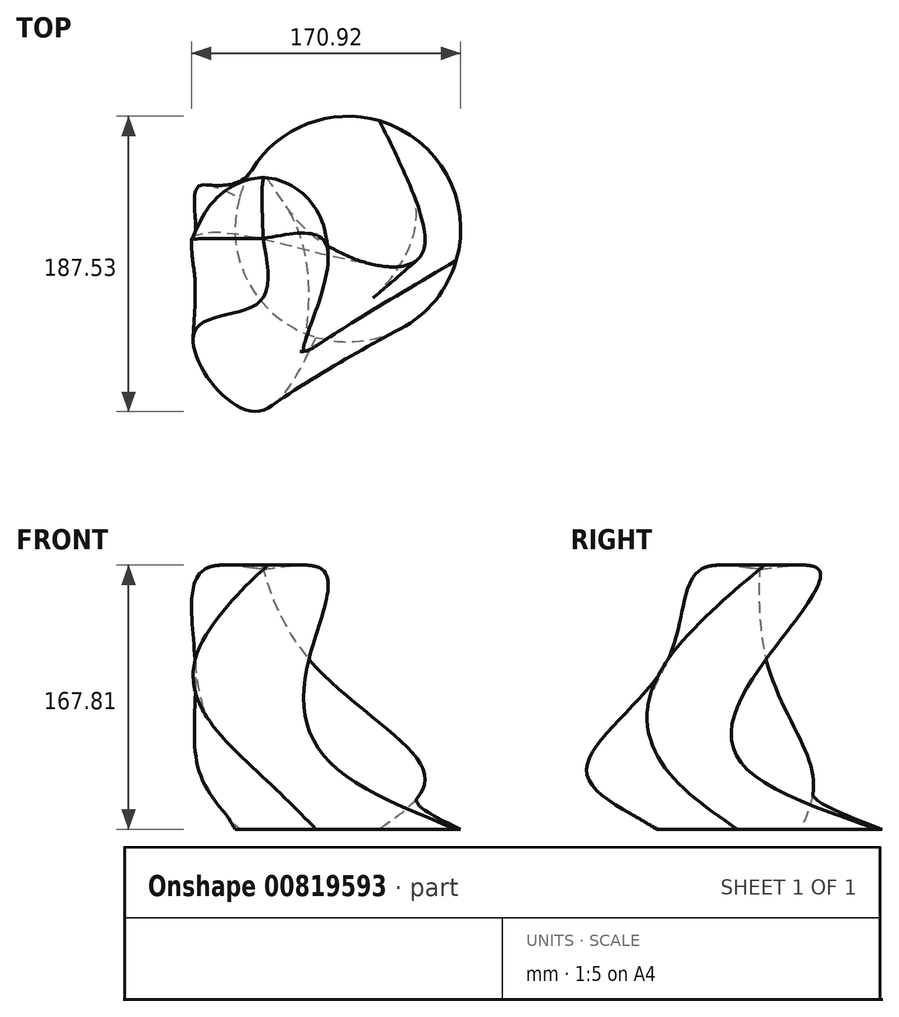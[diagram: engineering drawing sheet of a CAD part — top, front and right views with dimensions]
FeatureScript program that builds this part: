
annotation { "Feature Type Name" : "Feature", "Feature Type Description" : "" }
export const myFeature = defineFeature(function(context is Context, id is Id, definition is map)
    precondition{}
    {
        {
            var Q0;
            Q0=qCreatedBy(makeId("Top.planeOp"),FACE);
            cPlane(context, id + "F0", {"entities" : qUnion([Q0]), "cplaneType" : CPlaneType.OFFSET, "offset" : 108 * mm, "oppositeDirection" : true, "width" : 150 * mm, "height" : 150 * mm});
        }
        {
            var Q0;
            Q0=qCreatedBy(makeId("Top.planeOp"),FACE);
            cPlane(context, id + "F1", {"entities" : qUnion([Q0]), "cplaneType" : CPlaneType.OFFSET, "offset" : 72 * mm, "oppositeDirection" : true, "width" : 150 * mm, "height" : 150 * mm});
        }
        {
            var Q0;
            Q0=qCreatedBy(makeId("Top.planeOp"),FACE);
            cPlane(context, id + "F2", {"entities" : qUnion([Q0]), "cplaneType" : CPlaneType.OFFSET, "offset" : 57 * mm, "width" : 150 * mm, "height" : 150 * mm});
        }
        {
            var Q0;
            Q0=qCreatedBy(id+"F2.planeOp",FACE);
            var sketch = newSketch(context, id + "F3", { "sketchPlane" : qUnion([Q0])});
            skCircle(sketch, "E0", {"center": v(0, 38.13) * mm, "radius": 37.42 * mm});
            skSolve(sketch);
        }
        {
            var Q0;
            Q0=qCreatedBy(makeId("Top.planeOp"),FACE);
            var sketch = newSketch(context, id + "F4", { "sketchPlane" : qUnion([Q0])});
            skLineSegment(sketch, "E1.bottom", {"start": v(29, 42.26) * mm, "end": v(-43.2, 42.26) * mm});
            skLineSegment(sketch, "E1.top", {"start": v(29, -19.95) * mm, "end": v(-43.2, -19.95) * mm});
            skLineSegment(sketch, "E1.left", {"start": v(29, 42.26) * mm, "end": v(29, -19.95) * mm});
            skLineSegment(sketch, "E1.right", {"start": v(-43.2, 42.26) * mm, "end": v(-43.2, -19.95) * mm});
            skSolve(sketch);
        }
        {
            var Q0;
            Q0=qCreatedBy(id+"F1.planeOp",FACE);
            var sketch = newSketch(context, id + "F5", { "sketchPlane" : qUnion([Q0])});
            skCircle(sketch, "E2.cCircle", {"center": v(19.57, 10.78) * mm, "radius": 42.75 * mm, "construction": true});
            skLineSegment(sketch, "E2.0", {"start": v(-3.12, -71.64) * mm, "end": v(-40.47, 71.64) * mm});
            skLineSegment(sketch, "E2.1", {"start": v(-40.47, 71.64) * mm, "end": v(102.3, 32.34) * mm});
            skLineSegment(sketch, "E2.2", {"start": v(102.3, 32.34) * mm, "end": v(-3.12, -71.64) * mm});
            skPoint(sketch, "E2.0.midPoint", {"position": v(-21.8, 0) * mm});
            skSolve(sketch);
        }
        {
            var Q0;
            Q0=qCreatedBy(id+"F0.planeOp",FACE);
            var sketch = newSketch(context, id + "F6", { "sketchPlane" : qUnion([Q0])});
            skCircle(sketch, "E3", {"center": v(53.74, 44.14) * mm, "radius": 71.65 * mm});
            skSolve(sketch);
        }
        {
            var Q0;
            Q0=sQuery(id+"F3.wireOp",VERTEX,"E0.center");
            var Q1;
            Q1=makeQuery(id+"F3.imprint","IMPRINT",FACE,{"disambiguationData":[TD([[makeQuery(id+"F3.imprint","IMPRINT",EDGE,{"derivedFrom":sQuery(id+"F3.wireOp",EDGE,"E0")}),1.0]])]});
            var Q2;
            Q2=makeQuery(id+"F4.imprint","IMPRINT",FACE,{"disambiguationData":[TD([[makeQuery(id+"F4.imprint","IMPRINT",EDGE,{"derivedFrom":sQuery(id+"F4.wireOp",EDGE,"E1.bottom")}),1.0]])]});
            var Q3;
            Q3=makeQuery(id+"F5.imprint","IMPRINT",FACE,{"disambiguationData":[TD([[makeQuery(id+"F5.imprint","IMPRINT",EDGE,{"derivedFrom":sQuery(id+"F5.wireOp",EDGE,"E2.0")}),-1.0]])]});
            var Q4;
            Q4=makeQuery(id+"F6.imprint","IMPRINT",FACE,{"disambiguationData":[TD([[makeQuery(id+"F6.imprint","IMPRINT",EDGE,{"derivedFrom":sQuery(id+"F6.wireOp",EDGE,"E3")}),1.0]])]});
            loft(context, id + "F7", {"sheetProfilesArray" : [{ "sheetProfileEntities" : qUnion([Q0]) }, { "sheetProfileEntities" : qUnion([Q1]) }, { "sheetProfileEntities" : qUnion([Q2]) }, { "sheetProfileEntities" : qUnion([Q3]) }, { "sheetProfileEntities" : qUnion([Q4]) }]});
        }
    });
